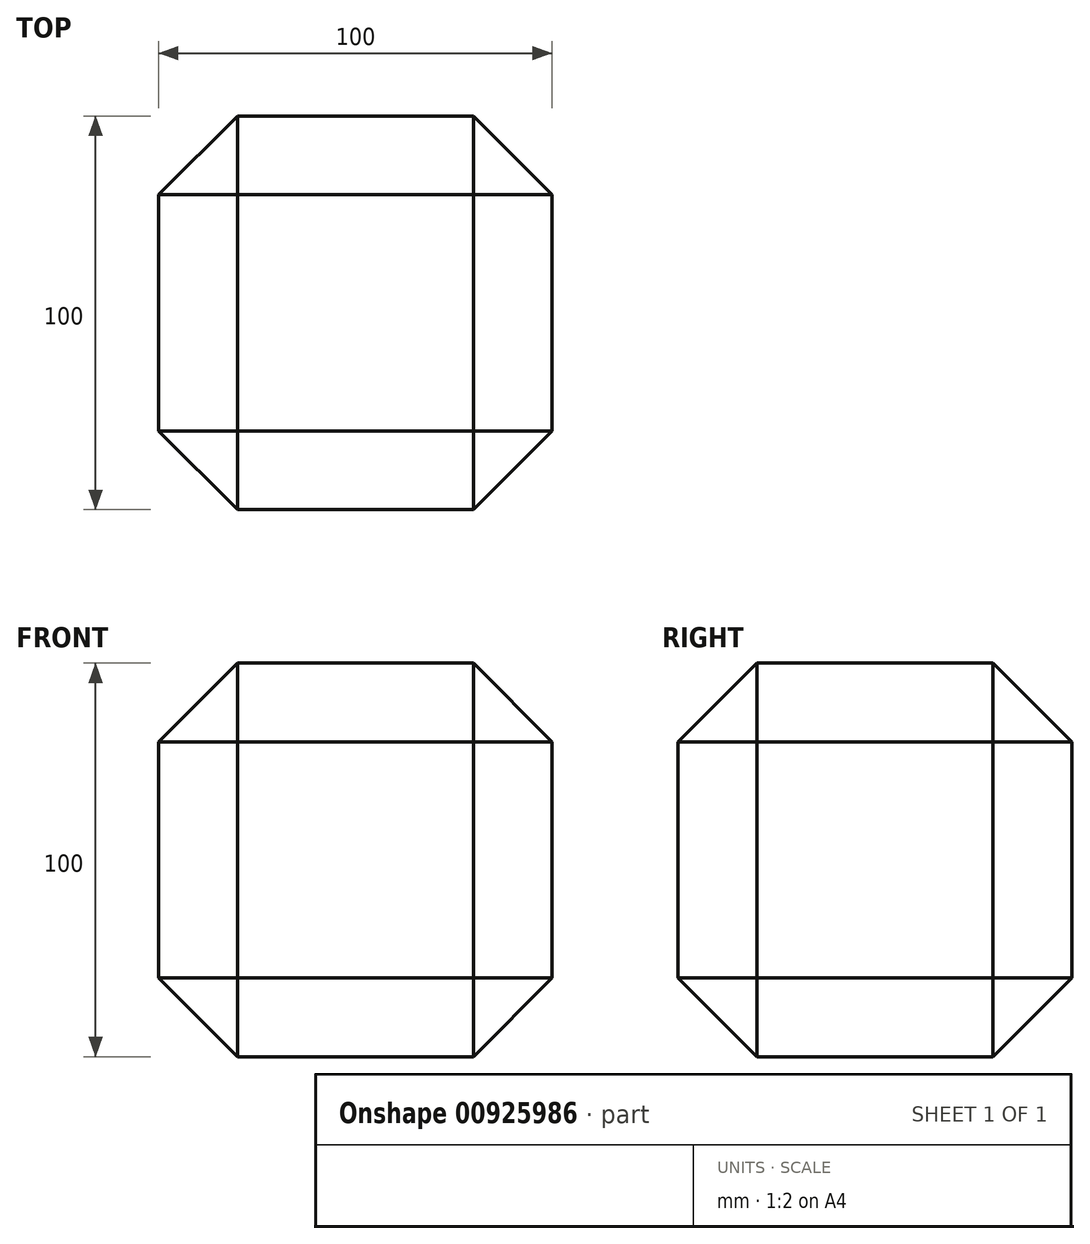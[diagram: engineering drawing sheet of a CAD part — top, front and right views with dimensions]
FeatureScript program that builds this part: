
annotation { "Feature Type Name" : "Feature", "Feature Type Description" : "" }
export const myFeature = defineFeature(function(context is Context, id is Id, definition is map)
    precondition{}
    {
        {
            var Q0;
            Q0=qCreatedBy(makeId("Top.planeOp"),FACE);
            var sketch = newSketch(context, id + "F0", { "sketchPlane" : qUnion([Q0])});
            skLineSegment(sketch, "E0.bottom", {"start": v(50, 50) * mm, "end": v(-50, 50) * mm});
            skLineSegment(sketch, "E0.top", {"start": v(50, -50) * mm, "end": v(-50, -50) * mm});
            skLineSegment(sketch, "E0.left", {"start": v(50, 50) * mm, "end": v(50, -50) * mm});
            skLineSegment(sketch, "E0.right", {"start": v(-50, 50) * mm, "end": v(-50, -50) * mm});
            skPoint(sketch, "E0.middle", {"position": v(0, 0) * mm});
            skSolve(sketch);
        }
        {
            var Q0;
            Q0=makeQuery(id+"F0.imprint","IMPRINT",FACE,{"disambiguationData":[TD([[makeQuery(id+"F0.imprint","IMPRINT",EDGE,{"derivedFrom":sQuery(id+"F0.wireOp",EDGE,"E0.bottom")}),1.0]])]});
            extrude(context, id + "F1", {"entities" : qUnion([Q0]), "depth" : 100 * mm, "offsetDistance" : 25 * mm});
        }
        {
            var Q0;
            Q0=makeQuery(id+"F1.opExtrude","CAP_EDGE",EDGE,{"disambiguationData":[OSD([sQuery(id+"F0.wireOp",EDGE,"E0.top")])],"isStart":false});
            var Q1;
            Q1=makeQuery(id+"F1.opExtrude","CAP_EDGE",EDGE,{"disambiguationData":[OSD([sQuery(id+"F0.wireOp",EDGE,"E0.left")])],"isStart":false});
            var Q2;
            Q2=makeQuery(id+"F1.opExtrude","CAP_EDGE",EDGE,{"disambiguationData":[OSD([sQuery(id+"F0.wireOp",EDGE,"E0.bottom")])],"isStart":false});
            var Q3;
            Q3=makeQuery(id+"F1.opExtrude","CAP_FACE",FACE,{"disambiguationData":[OSD([sQuery(id+"F0.wireOp",EDGE,"E0.bottom"),sQuery(id+"F0.wireOp",EDGE,"E0.top"),sQuery(id+"F0.wireOp",EDGE,"E0.left"),sQuery(id+"F0.wireOp",EDGE,"E0.right")])],"isStart":false});
            var Q4;
            Q4=makeQuery(id+"F1.opExtrude","CAP_FACE",FACE,{"disambiguationData":[OSD([sQuery(id+"F0.wireOp",EDGE,"E0.bottom"),sQuery(id+"F0.wireOp",EDGE,"E0.top"),sQuery(id+"F0.wireOp",EDGE,"E0.left"),sQuery(id+"F0.wireOp",EDGE,"E0.right")])],"isStart":true});
            var Q5;
            Q5=makeQuery(id+"F1.opExtrude","SWEPT_FACE",FACE,{"disambiguationData":[OSD([sQuery(id+"F0.wireOp",EDGE,"E0.left")])]});
            var Q6;
            Q6=makeQuery(id+"F1.opExtrude","SWEPT_FACE",FACE,{"disambiguationData":[OSD([sQuery(id+"F0.wireOp",EDGE,"E0.right")])]});
            chamfer(context, id + "F2", {"entities" : qUnion([Q0, Q1, Q2, Q3, Q4, Q5, Q6]), "width" : 20 * mm, "tangentPropagation" : true});
        }
    });
